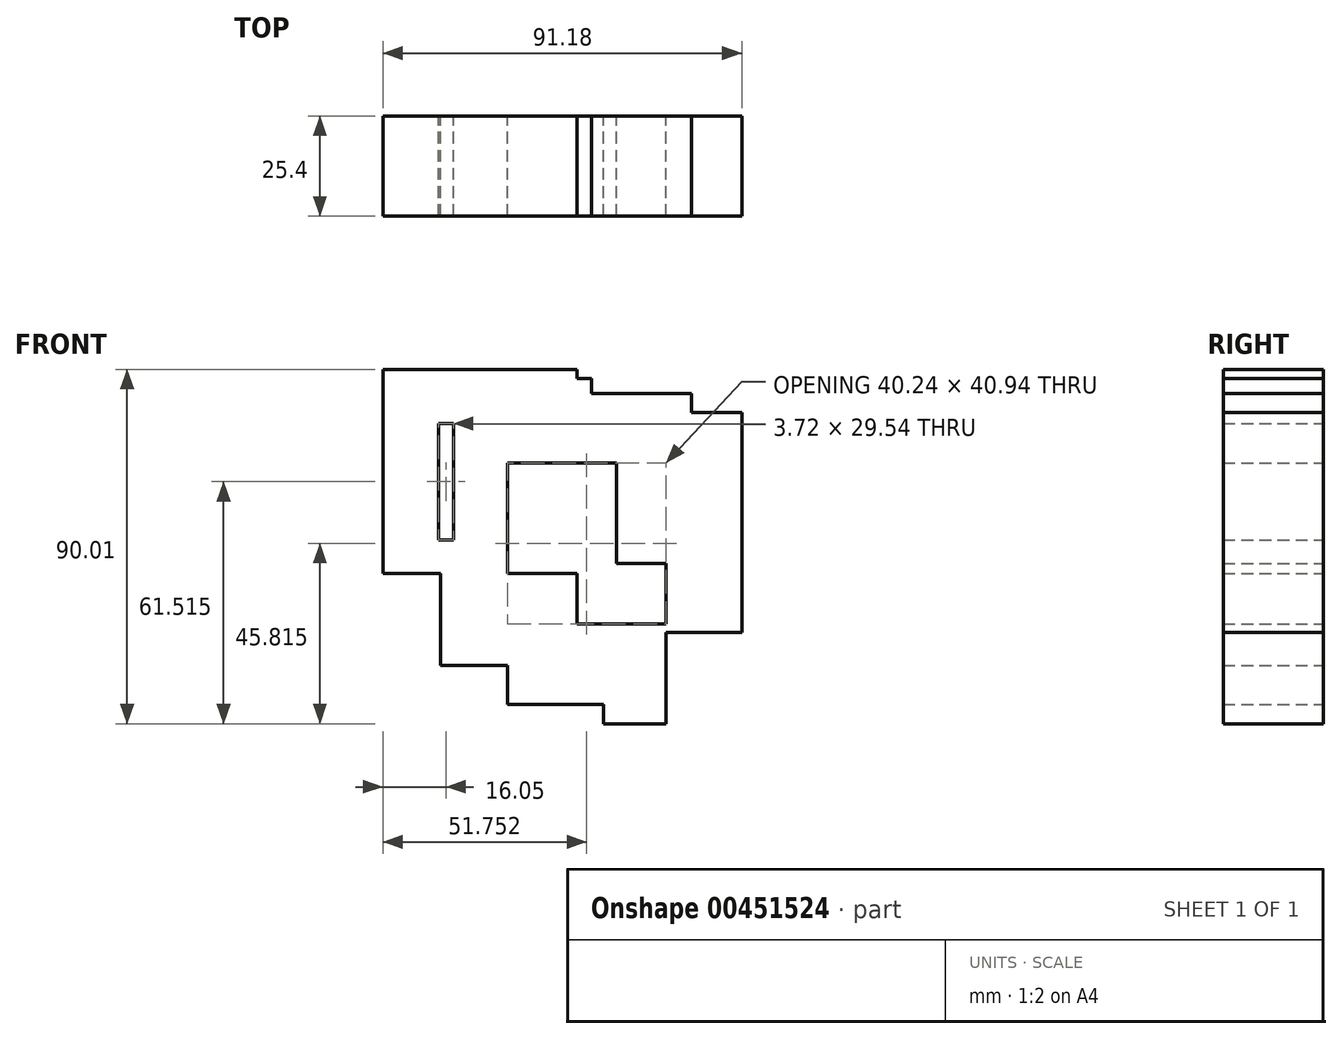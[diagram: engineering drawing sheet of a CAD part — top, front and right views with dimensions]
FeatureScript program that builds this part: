
annotation { "Feature Type Name" : "Feature", "Feature Type Description" : "" }
export const myFeature = defineFeature(function(context is Context, id is Id, definition is map)
    precondition{}
    {
        {
            var Q0;
            Q0=qCreatedBy(makeId("Front.planeOp"),FACE);
            var sketch = newSketch(context, id + "F0", { "sketchPlane" : qUnion([Q0])});
            skLineSegment(sketch, "E0.bottom", {"start": v(0, 0) * mm, "end": v(-49.3, 0) * mm});
            skLineSegment(sketch, "E0.top", {"start": v(0, 51.87) * mm, "end": v(-49.3, 51.87) * mm});
            skLineSegment(sketch, "E0.left", {"start": v(0, 0) * mm, "end": v(0, 51.87) * mm});
            skLineSegment(sketch, "E0.right", {"start": v(-49.3, 0) * mm, "end": v(-49.3, 51.87) * mm});
            skLineSegment(sketch, "E1.bottom", {"start": v(-35.12, 49.54) * mm, "end": v(3.72, 49.54) * mm});
            skLineSegment(sketch, "E1.top", {"start": v(-35.12, 0) * mm, "end": v(3.72, 0) * mm});
            skLineSegment(sketch, "E1.left", {"start": v(-35.12, 49.54) * mm, "end": v(-35.12, 0) * mm});
            skLineSegment(sketch, "E1.right", {"start": v(3.72, 49.54) * mm, "end": v(3.72, 0) * mm});
            skLineSegment(sketch, "E2.bottom", {"start": v(-13.72, 35.35) * mm, "end": v(-34.66, 35.35) * mm});
            skLineSegment(sketch, "E2.top", {"start": v(-13.72, -23.26) * mm, "end": v(-34.66, -23.26) * mm});
            skLineSegment(sketch, "E2.left", {"start": v(-13.72, 35.35) * mm, "end": v(-13.72, -23.26) * mm});
            skLineSegment(sketch, "E2.right", {"start": v(-34.66, 35.35) * mm, "end": v(-34.66, -23.26) * mm});
            skLineSegment(sketch, "E3.bottom", {"start": v(-17.68, 28.14) * mm, "end": v(10, 28.14) * mm});
            skLineSegment(sketch, "E3.top", {"start": v(-17.68, -33.26) * mm, "end": v(10, -33.26) * mm});
            skLineSegment(sketch, "E3.left", {"start": v(-17.68, 28.14) * mm, "end": v(-17.68, -33.26) * mm});
            skLineSegment(sketch, "E3.right", {"start": v(10, 28.14) * mm, "end": v(10, -33.26) * mm});
            skLineSegment(sketch, "E4.bottom", {"start": v(0, 45.82) * mm, "end": v(29.07, 45.82) * mm});
            skLineSegment(sketch, "E4.top", {"start": v(0, -12.8) * mm, "end": v(29.07, -12.8) * mm});
            skLineSegment(sketch, "E4.left", {"start": v(0, 45.82) * mm, "end": v(0, -12.8) * mm});
            skLineSegment(sketch, "E4.right", {"start": v(29.07, 45.82) * mm, "end": v(29.07, -12.8) * mm});
            skLineSegment(sketch, "E5.bottom", {"start": v(17.21, 40.94) * mm, "end": v(41.87, 40.94) * mm});
            skLineSegment(sketch, "E5.top", {"start": v(17.21, -14.89) * mm, "end": v(41.87, -14.89) * mm});
            skLineSegment(sketch, "E5.left", {"start": v(17.21, 40.94) * mm, "end": v(17.21, -14.89) * mm});
            skLineSegment(sketch, "E5.right", {"start": v(41.87, 40.94) * mm, "end": v(41.87, -14.89) * mm});
            skLineSegment(sketch, "E6.bottom", {"start": v(6.75, 2.56) * mm, "end": v(22.56, 2.56) * mm});
            skLineSegment(sketch, "E6.top", {"start": v(6.75, -38.14) * mm, "end": v(22.56, -38.14) * mm});
            skLineSegment(sketch, "E6.left", {"start": v(6.75, 2.56) * mm, "end": v(6.75, -38.14) * mm});
            skLineSegment(sketch, "E6.right", {"start": v(22.56, 2.56) * mm, "end": v(22.56, -38.14) * mm});
            skLineSegment(sketch, "E7.bottom", {"start": v(-5.81, 24.65) * mm, "end": v(-9.3, 24.65) * mm});
            skLineSegment(sketch, "E7.top", {"start": v(-5.81, 0) * mm, "end": v(-9.3, 0) * mm});
            skLineSegment(sketch, "E7.left", {"start": v(-5.81, 24.65) * mm, "end": v(-5.81, 0) * mm});
            skLineSegment(sketch, "E7.right", {"start": v(-9.3, 24.65) * mm, "end": v(-9.3, 0) * mm});
            skLineSegment(sketch, "E8.bottom", {"start": v(-31.4, 38.14) * mm, "end": v(-49.3, 38.14) * mm});
            skLineSegment(sketch, "E8.top", {"start": v(-31.4, 8.6) * mm, "end": v(-49.3, 8.6) * mm});
            skLineSegment(sketch, "E8.left", {"start": v(-31.4, 38.14) * mm, "end": v(-31.4, 8.6) * mm});
            skLineSegment(sketch, "E8.right", {"start": v(-49.3, 38.14) * mm, "end": v(-49.3, 8.6) * mm});
            skSolve(sketch);
        }
        {
            var Q0;
            Q0 = qSketchRegion(id + "F0", true);
            extrude(context, id + "F1", {"entities" : qUnion([Q0]), "depth" : 25.4 * mm});
        }
    });
